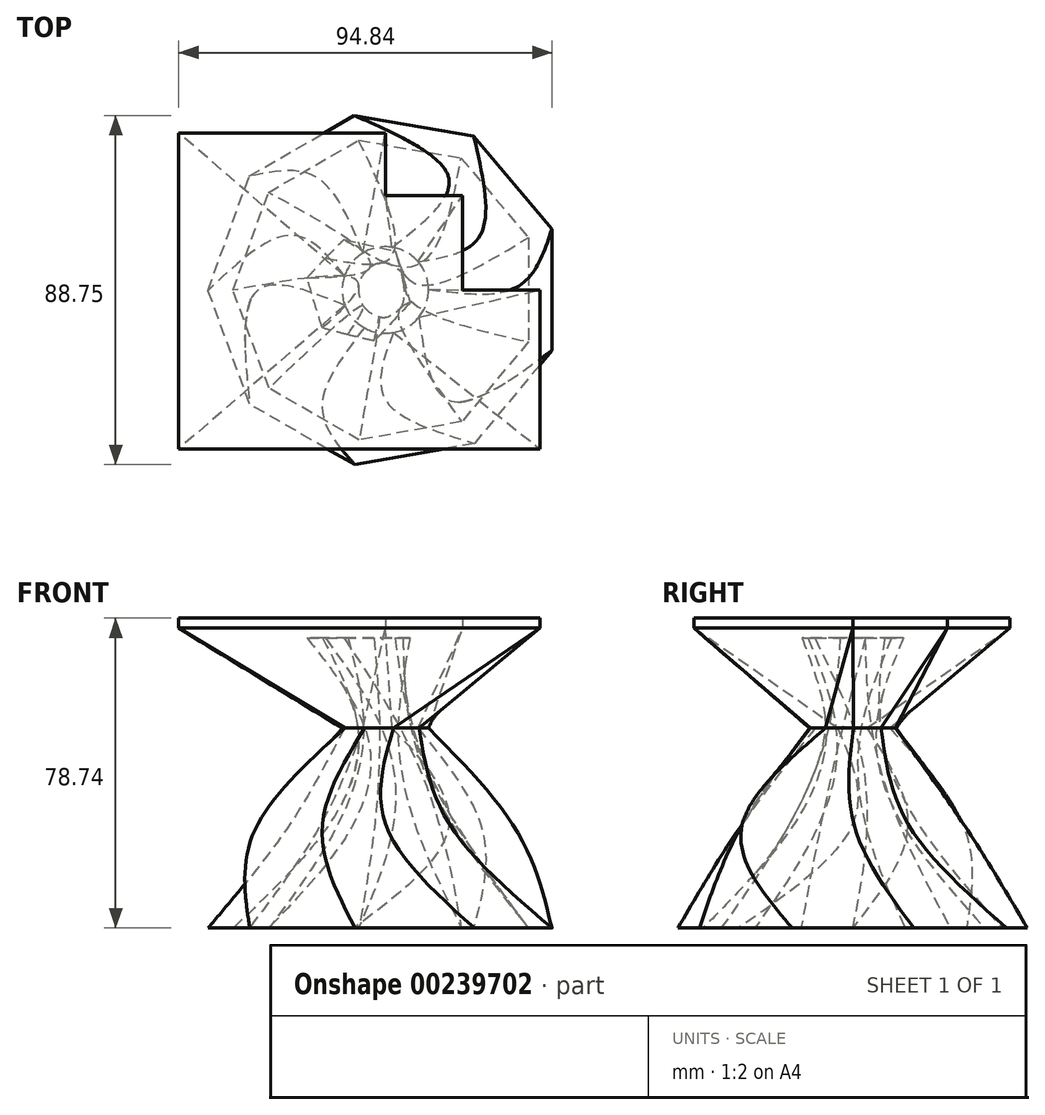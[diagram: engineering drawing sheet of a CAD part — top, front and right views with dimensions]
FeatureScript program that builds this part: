
annotation { "Feature Type Name" : "Feature", "Feature Type Description" : "" }
export const myFeature = defineFeature(function(context is Context, id is Id, definition is map)
    precondition{}
    {
        {
            var Q0;
            Q0=qCreatedBy(makeId("Top.planeOp"),FACE);
            var sketch = newSketch(context, id + "F0", { "sketchPlane" : qUnion([Q0])});
            skCircle(sketch, "E0.cCircle", {"center": v(0, 0) * mm, "radius": 28.54 * mm, "construction": true});
            skLineSegment(sketch, "E0.0", {"start": v(32.95, 0.53) * mm, "end": v(16.93, -28.28) * mm});
            skLineSegment(sketch, "E0.1", {"start": v(16.93, -28.28) * mm, "end": v(-16.02, -28.8) * mm});
            skLineSegment(sketch, "E0.2", {"start": v(-16.02, -28.8) * mm, "end": v(-32.95, -0.53) * mm});
            skLineSegment(sketch, "E0.3", {"start": v(-32.95, -0.53) * mm, "end": v(-16.93, 28.28) * mm});
            skLineSegment(sketch, "E0.4", {"start": v(-16.93, 28.28) * mm, "end": v(16.02, 28.8) * mm});
            skLineSegment(sketch, "E0.5", {"start": v(16.02, 28.8) * mm, "end": v(32.95, 0.53) * mm});
            skPoint(sketch, "E0.0.midPoint", {"position": v(24.94, -13.87) * mm});
            skSolve(sketch);
        }
        {
            var Q0;
            Q0=qCreatedBy(makeId("Top.planeOp"),FACE);
            cPlane(context, id + "F1", {"entities" : qUnion([Q0]), "cplaneType" : CPlaneType.OFFSET, "offset" : 25.4 * mm, "width" : 152.4 * mm, "height" : 152.4 * mm});
        }
        {
            var Q0;
            Q0=qCreatedBy(makeId("Top.planeOp"),FACE);
            cPlane(context, id + "F2", {"entities" : qUnion([Q0]), "cplaneType" : CPlaneType.OFFSET, "offset" : 25.4 * mm, "oppositeDirection" : true, "width" : 152.4 * mm, "height" : 152.4 * mm});
        }
        {
            var Q0;
            Q0=qCreatedBy(id+"F1.planeOp",FACE);
            var sketch = newSketch(context, id + "F3", { "sketchPlane" : qUnion([Q0])});
            skCircle(sketch, "E1", {"center": v(0, 0) * mm, "radius": 10.98 * mm});
            skSolve(sketch);
        }
        {
            var Q0;
            Q0=qCreatedBy(id+"F2.planeOp",FACE);
            var sketch = newSketch(context, id + "F4", { "sketchPlane" : qUnion([Q0])});
            skCircle(sketch, "E2.cCircle", {"center": v(0, 0) * mm, "radius": 45.06 * mm, "construction": true});
            skLineSegment(sketch, "E2.0", {"start": v(22.6, -38.97) * mm, "end": v(-7.74, -44.39) * mm});
            skLineSegment(sketch, "E2.1", {"start": v(-7.74, -44.39) * mm, "end": v(-34.46, -29.03) * mm});
            skLineSegment(sketch, "E2.2", {"start": v(-34.46, -29.03) * mm, "end": v(-45.06, -0.09) * mm});
            skLineSegment(sketch, "E2.3", {"start": v(-45.06, -0.09) * mm, "end": v(-34.57, 28.9) * mm});
            skLineSegment(sketch, "E2.4", {"start": v(-34.57, 28.9) * mm, "end": v(-7.91, 44.36) * mm});
            skLineSegment(sketch, "E2.5", {"start": v(-7.91, 44.36) * mm, "end": v(22.45, 39.06) * mm});
            skLineSegment(sketch, "E2.6", {"start": v(22.45, 39.06) * mm, "end": v(42.3, 15.5) * mm});
            skLineSegment(sketch, "E2.7", {"start": v(42.3, 15.5) * mm, "end": v(42.37, -15.33) * mm});
            skLineSegment(sketch, "E2.8", {"start": v(42.37, -15.33) * mm, "end": v(22.6, -38.97) * mm});
            skSolve(sketch);
        }
        {
            var Q0;
            Q0=makeQuery(id+"F3.imprint","IMPRINT",FACE,{"disambiguationData":[TD([[makeQuery(id+"F3.imprint","IMPRINT",EDGE,{"derivedFrom":sQuery(id+"F3.wireOp",EDGE,"E1")}),1.0]])]});
            var Q1;
            Q1=makeQuery(id+"F0.imprint","IMPRINT",FACE,{"disambiguationData":[TD([[makeQuery(id+"F0.imprint","IMPRINT",EDGE,{"derivedFrom":sQuery(id+"F0.wireOp",EDGE,"E0.0")}),-1.0]])]});
            var Q2;
            Q2=makeQuery(id+"F4.imprint","IMPRINT",FACE,{"disambiguationData":[TD([[makeQuery(id+"F4.imprint","IMPRINT",EDGE,{"derivedFrom":sQuery(id+"F4.wireOp",EDGE,"E2.0")}),-1.0]])]});
            loft(context, id + "F5", {"sheetProfilesArray" : [{ "sheetProfileEntities" : qUnion([Q0]) }, { "sheetProfileEntities" : qUnion([Q1]) }, { "sheetProfileEntities" : qUnion([Q2]) }]});
        }
        {
            var Q0;
            Q0=makeQuery(id+"F5.opLoft","CAP_FACE",FACE,{"disambiguationData":[OSD([makeQuery(id+"F3.imprint","IMPRINT",FACE,{"disambiguationData":[TD([[makeQuery(id+"F3.imprint","IMPRINT",EDGE,{"derivedFrom":sQuery(id+"F3.wireOp",EDGE,"E1")}),1.0]])]})])],"isStart":true});
            var sketch = newSketch(context, id + "F6", { "sketchPlane" : qUnion([Q0])});
            skSolve(sketch);
        }
        {
            var Q0;
            Q0=qCreatedBy(id+"F1.planeOp",FACE);
            cPlane(context, id + "F7", {"entities" : qUnion([Q0]), "cplaneType" : CPlaneType.OFFSET, "offset" : 25.4 * mm, "width" : 152.4 * mm, "height" : 152.4 * mm});
        }
        {
            var Q0;
            Q0=qCreatedBy(id+"F7.planeOp",FACE);
            var sketch = newSketch(context, id + "F8", { "sketchPlane" : qUnion([Q0])});
            skLineSegment(sketch, "E3.bottom", {"start": v(19.62, 0) * mm, "end": v(39.24, 0) * mm});
            skLineSegment(sketch, "E3.top", {"start": v(0, -40.35) * mm, "end": v(39.24, -40.35) * mm});
            skLineSegment(sketch, "E3.right", {"start": v(39.24, 0) * mm, "end": v(39.24, -40.35) * mm});
            skLineSegment(sketch, "E4.bottom", {"start": v(0, -40.35) * mm, "end": v(-52.47, -40.35) * mm});
            skLineSegment(sketch, "E4.top", {"start": v(0, 39.9) * mm, "end": v(-52.47, 39.9) * mm});
            skLineSegment(sketch, "E4.left", {"start": v(0, 0) * mm, "end": v(0, 39.9) * mm});
            skLineSegment(sketch, "E4.right", {"start": v(-52.47, -40.35) * mm, "end": v(-52.47, 39.9) * mm});
            skLineSegment(sketch, "E5.top", {"start": v(19.62, 24.03) * mm, "end": v(0, 24.03) * mm});
            skLineSegment(sketch, "E5.left", {"start": v(19.62, 0) * mm, "end": v(19.62, 24.03) * mm});
            skPoint(sketch, "E3.left.start.orphan", {"position": v(0, 0) * mm});
            skSolve(sketch);
        }
        {
            var Q1;
            {var subQ0=sQuery(id+"F4.wireOp",EDGE,"E2.8");var subQ2=sQuery(id+"F4.wireOp",EDGE,"E2.0");var subQ3=sQuery(id+"F3.wireOp",EDGE,"E1");var subQ4=sQuery(id+"F4.wireOp",EDGE,"E2.1");Q1=makeQuery(id+"F6.imprint","IMPRINT",FACE,{"disambiguationData":[TD([[makeQuery(id+"F6.imprint","IMPRINT",EDGE,{"derivedFrom":makeQuery(id+"F5.opLoft","MID_CAP_EDGE",EDGE,{"disambiguationData":[OSD([subQ3,subQ2,subQ4,subQ0])],"capPos":0.0})}),1.0]])]});}
            var Q2;
            Q2=makeQuery(id+"F8.imprint","IMPRINT",FACE,{"disambiguationData":[TD([[makeQuery(id+"F8.imprint","IMPRINT",EDGE,{"derivedFrom":sQuery(id+"F8.wireOp",EDGE,"E3.bottom")}),-1.0]])]});
            loft(context, id + "F9", {"operationType" : NewBodyOperationType.ADD, "sheetProfilesArray" : [{ "sheetProfileEntities" : qUnion([Q1]) }, { "sheetProfileEntities" : qUnion([Q2]) }]});
        }
        {
            var Q0;
            Q0=makeQuery(id+"F5.opLoft","CAP_FACE",FACE,{"disambiguationData":[OSD([makeQuery(id+"F4.imprint","IMPRINT",FACE,{"disambiguationData":[TD([[makeQuery(id+"F4.imprint","IMPRINT",EDGE,{"derivedFrom":sQuery(id+"F4.wireOp",EDGE,"E2.0")}),-1.0]])]})])],"isStart":true});
            var sketch = newSketch(context, id + "F10", { "sketchPlane" : qUnion([Q0])});
            skLineSegment(sketch, "E6.0", {"start": v(36.31, -13.3) * mm, "end": v(36.36, 13.15) * mm});
            skLineSegment(sketch, "E6.1", {"start": v(19.27, -33.53) * mm, "end": v(36.31, -13.3) * mm});
            skLineSegment(sketch, "E6.2", {"start": v(36.36, 13.15) * mm, "end": v(19.4, 33.45) * mm});
            skLineSegment(sketch, "E6.3", {"start": v(-6.8, -38.07) * mm, "end": v(19.27, -33.53) * mm});
            skLineSegment(sketch, "E6.4", {"start": v(-29.67, -24.8) * mm, "end": v(-6.8, -38.07) * mm});
            skLineSegment(sketch, "E6.5", {"start": v(19.4, 33.45) * mm, "end": v(-6.64, 38.1) * mm});
            skLineSegment(sketch, "E6.6", {"start": v(-6.64, 38.1) * mm, "end": v(-29.57, 24.92) * mm});
            skLineSegment(sketch, "E6.7", {"start": v(-29.57, 24.92) * mm, "end": v(-38.67, 0.08) * mm});
            skLineSegment(sketch, "E6.8", {"start": v(-38.67, 0.08) * mm, "end": v(-29.67, -24.8) * mm});
            skSolve(sketch);
        }
        {
            var Q0;
            Q0=qCreatedBy(id+"F1.planeOp",FACE);
            var sketch = newSketch(context, id + "F11", { "sketchPlane" : qUnion([Q0])});
            skCircle(sketch, "E7", {"center": v(0, 0) * mm, "radius": 7 * mm});
            skSolve(sketch);
        }
        {
            var Q0;
            Q0=makeQuery(id+"F9.opLoft","CAP_FACE",FACE,{"disambiguationData":[OSD([makeQuery(id+"F8.imprint","IMPRINT",FACE,{"disambiguationData":[TD([[makeQuery(id+"F8.imprint","IMPRINT",EDGE,{"derivedFrom":sQuery(id+"F8.wireOp",EDGE,"E3.bottom")}),-1.0]])]})])],"isStart":true});
            var sketch = newSketch(context, id + "F12", { "sketchPlane" : qUnion([Q0])});
            skCircle(sketch, "E8.cCircle", {"center": v(-7.59, 0) * mm, "radius": 12.7 * mm, "construction": true});
            skLineSegment(sketch, "E8.0", {"start": v(-3.04, -13.94) * mm, "end": v(-17.39, -10.91) * mm});
            skLineSegment(sketch, "E8.1", {"start": v(-17.39, -10.91) * mm, "end": v(-21.94, 3.03) * mm});
            skLineSegment(sketch, "E8.2", {"start": v(-21.94, 3.03) * mm, "end": v(-12.14, 13.94) * mm});
            skLineSegment(sketch, "E8.3", {"start": v(-12.14, 13.94) * mm, "end": v(2.2, 10.91) * mm});
            skLineSegment(sketch, "E8.4", {"start": v(2.2, 10.91) * mm, "end": v(6.76, -3.03) * mm});
            skLineSegment(sketch, "E8.5", {"start": v(6.76, -3.03) * mm, "end": v(-3.04, -13.94) * mm});
            skPoint(sketch, "E8.0.midPoint", {"position": v(-10.21, -12.43) * mm});
            skSolve(sketch);
        }
        {
            var Q1;
            Q1=makeQuery(id+"F12.imprint","IMPRINT",FACE,{"disambiguationData":[TD([[makeQuery(id+"F12.imprint","IMPRINT",EDGE,{"derivedFrom":sQuery(id+"F12.wireOp",EDGE,"E8.0")}),-1.0]])]});
            var Q2;
            Q2=makeQuery(id+"F11.imprint","IMPRINT",FACE,{"disambiguationData":[TD([[makeQuery(id+"F11.imprint","IMPRINT",EDGE,{"derivedFrom":sQuery(id+"F11.wireOp",EDGE,"E7")}),1.0]])]});
            var Q3;
            Q3=makeQuery(id+"F10.imprint","IMPRINT",FACE,{"disambiguationData":[TD([[makeQuery(id+"F10.imprint","IMPRINT",EDGE,{"derivedFrom":sQuery(id+"F10.wireOp",EDGE,"E6.0")}),1.0]])]});
            loft(context, id + "F13", {"operationType" : NewBodyOperationType.REMOVE, "sheetProfilesArray" : [{ "sheetProfileEntities" : qUnion([Q1]) }, { "sheetProfileEntities" : qUnion([Q2]) }, { "sheetProfileEntities" : qUnion([Q3]) }]});
        }
        {
            var Q0;
            Q0=makeQuery(id+"F9.opLoft","CAP_FACE",FACE,{"disambiguationData":[OSD([makeQuery(id+"F8.imprint","IMPRINT",FACE,{"disambiguationData":[TD([[makeQuery(id+"F8.imprint","IMPRINT",EDGE,{"derivedFrom":sQuery(id+"F8.wireOp",EDGE,"E3.bottom")}),-1.0]])]})])],"isStart":true});
            extrude(context, id + "F14", {"entities" : qUnion([Q0]), "operationType" : NewBodyOperationType.ADD, "depth" : 2.54 * mm});
        }
        {
            var Q0;
            Q0=makeQuery(id+"F14.opExtrude","CAP_FACE",FACE,{"disambiguationData":[OSD([makeQuery(id+"F8.imprint","IMPRINT",FACE,{"disambiguationData":[TD([[makeQuery(id+"F8.imprint","IMPRINT",EDGE,{"derivedFrom":sQuery(id+"F8.wireOp",EDGE,"E3.bottom")}),-1.0]])]})])],"isStart":false});
            var sketch = newSketch(context, id + "F15", { "sketchPlane" : qUnion([Q0])});
            skCircle(sketch, "E9.cCircle", {"center": v(-7.4, 2.82) * mm, "radius": 18.33 * mm, "construction": true});
            skLineSegment(sketch, "E9.0", {"start": v(12.7, -3.8) * mm, "end": v(-3.09, -17.9) * mm});
            skLineSegment(sketch, "E9.1", {"start": v(-3.09, -17.9) * mm, "end": v(-23.18, -11.27) * mm});
            skLineSegment(sketch, "E9.2", {"start": v(-23.18, -11.27) * mm, "end": v(-27.5, 9.44) * mm});
            skLineSegment(sketch, "E9.3", {"start": v(-27.5, 9.44) * mm, "end": v(-11.7, 23.53) * mm});
            skLineSegment(sketch, "E9.4", {"start": v(-11.7, 23.53) * mm, "end": v(8.39, 16.9) * mm});
            skLineSegment(sketch, "E9.5", {"start": v(8.39, 16.9) * mm, "end": v(12.7, -3.8) * mm});
            skPoint(sketch, "E9.0.midPoint", {"position": v(4.8, -10.85) * mm});
            skSolve(sketch);
        }
        {
            var Q0;
            Q0 = qSketchRegion(id + "F15", true);
            extrude(context, id + "F16", {"entities" : qUnion([Q0]), "operationType" : NewBodyOperationType.ADD, "oppositeDirection" : true, "depth" : 5.08 * mm});
        }
    });
